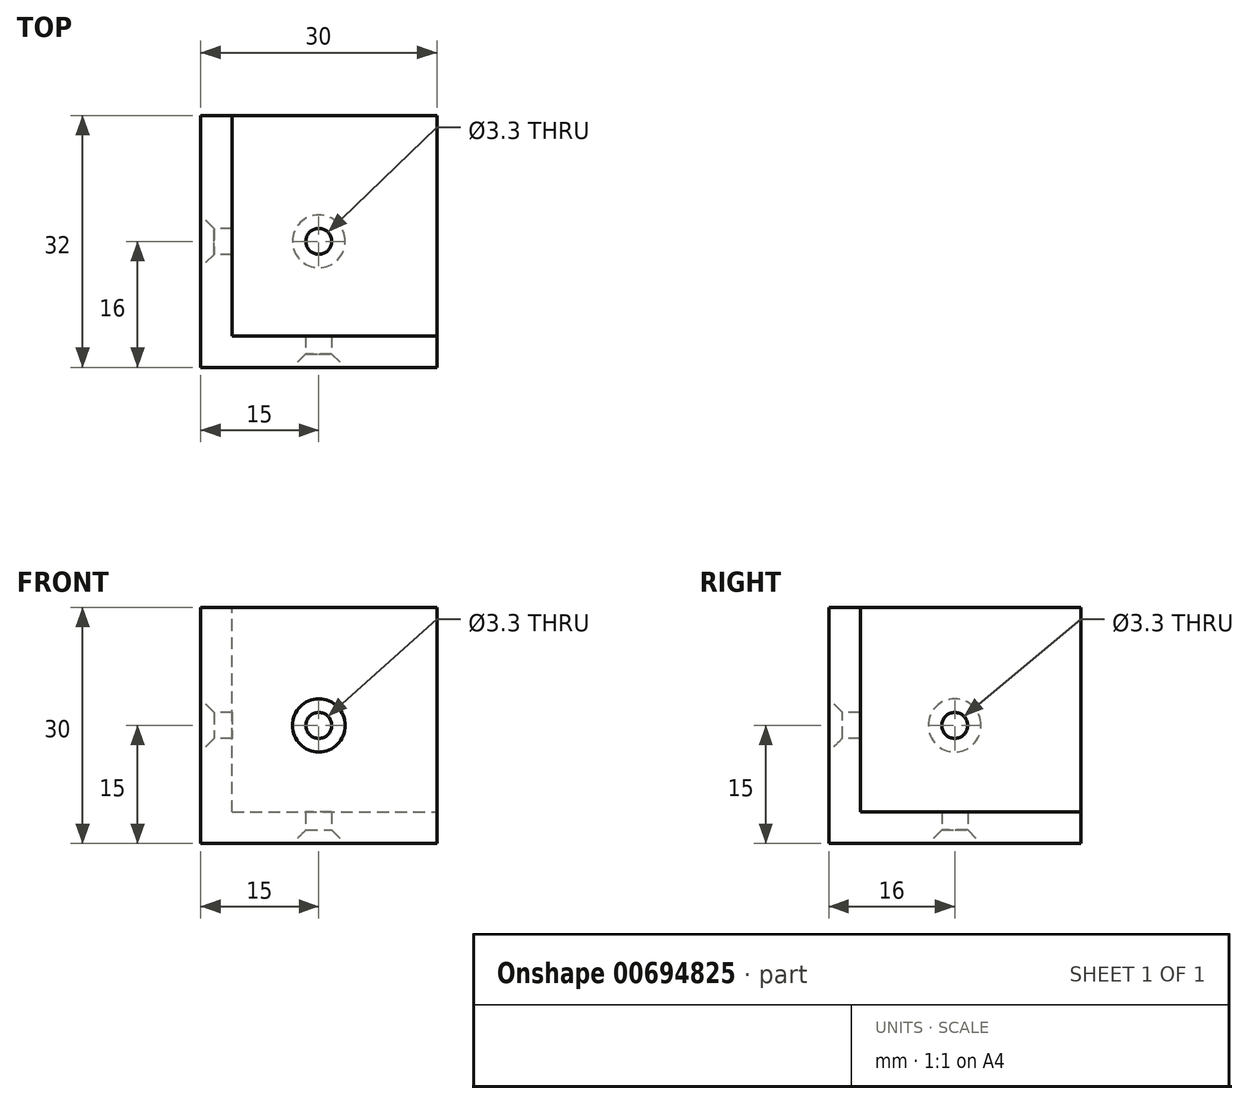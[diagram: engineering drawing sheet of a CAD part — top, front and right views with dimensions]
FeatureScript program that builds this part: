
annotation { "Feature Type Name" : "Feature", "Feature Type Description" : "" }
export const myFeature = defineFeature(function(context is Context, id is Id, definition is map)
    precondition{}
    {
        {
            var Q0;
            Q0=qCreatedBy(makeId("Front.planeOp"),FACE);
            var sketch = newSketch(context, id + "F0", { "sketchPlane" : qUnion([Q0])});
            skLineSegment(sketch, "E0.bottom", {"start": v(0, 0) * mm, "end": v(4, 0) * mm});
            skLineSegment(sketch, "E0.top", {"start": v(0, 30) * mm, "end": v(4, 30) * mm});
            skLineSegment(sketch, "E0.left", {"start": v(0, 0) * mm, "end": v(0, 30) * mm});
            skLineSegment(sketch, "E0.right", {"start": v(4, 4) * mm, "end": v(4, 30) * mm});
            skLineSegment(sketch, "E1.bottom", {"start": v(0, 0) * mm, "end": v(30, 0) * mm});
            skLineSegment(sketch, "E1.top", {"start": v(4, 4) * mm, "end": v(30, 4) * mm});
            skLineSegment(sketch, "E1.left", {"start": v(0, 0) * mm, "end": v(0, 4) * mm});
            skLineSegment(sketch, "E1.right", {"start": v(30, 0) * mm, "end": v(30, 4) * mm});
            skSolve(sketch);
        }
        {
            var Q0;
            Q0 = qSketchRegion(id + "F0", true);
            extrude(context, id + "F1", {"entities" : qUnion([Q0]), "depth" : 28 * mm, "offsetDistance" : 25 * mm});
        }
        {
            var Q0;
            Q0=makeQuery(id+"F1.opExtrude","CAP_FACE",FACE,{"disambiguationData":[OSD([sQuery(id+"F0.wireOp",EDGE,"E0.top"),sQuery(id+"F0.wireOp",EDGE,"E0.left"),sQuery(id+"F0.wireOp",EDGE,"E0.right"),sQuery(id+"F0.wireOp",EDGE,"E1.bottom"),sQuery(id+"F0.wireOp",EDGE,"E1.top"),sQuery(id+"F0.wireOp",EDGE,"E1.left"),sQuery(id+"F0.wireOp",EDGE,"E1.right")])],"isStart":false});
            var sketch = newSketch(context, id + "F2", { "sketchPlane" : qUnion([Q0])});
            skLineSegment(sketch, "E2.bottom", {"start": v(0, 0) * mm, "end": v(30, 0) * mm});
            skLineSegment(sketch, "E2.top", {"start": v(0, 30) * mm, "end": v(30, 30) * mm});
            skLineSegment(sketch, "E2.left", {"start": v(0, 0) * mm, "end": v(0, 30) * mm});
            skLineSegment(sketch, "E2.right", {"start": v(30, 0) * mm, "end": v(30, 30) * mm});
            skSolve(sketch);
        }
        {
            var Q0;
            Q0 = qSketchRegion(id + "F2", true);
            extrude(context, id + "F3", {"entities" : qUnion([Q0]), "operationType" : NewBodyOperationType.ADD, "depth" : 4 * mm, "offsetDistance" : 25 * mm});
        }
        {
            var Q0;
            Q0=makeQuery(id+"F3.opExtrude","CAP_FACE",FACE,{"disambiguationData":[OSD([sQuery(id+"F2.wireOp",EDGE,"E2.bottom"),sQuery(id+"F2.wireOp",EDGE,"E2.top"),sQuery(id+"F2.wireOp",EDGE,"E2.left"),sQuery(id+"F2.wireOp",EDGE,"E2.right")])],"isStart":false});
            var sketch = newSketch(context, id + "F4", { "sketchPlane" : qUnion([Q0])});
            skLineSegment(sketch, "E3", {"start": v(0, 0) * mm, "end": v(30, 30) * mm});
            skPoint(sketch, "E4", {"position": v(15, 15) * mm});
            skSolve(sketch);
        }
        {
            var Q0;
            Q0=sQuery(id+"F4.wireOp",VERTEX,"E4");
            var Q1;
            Q1=makeQuery(id+"F1.opExtrude","SWEPT_BODY",BODY,{"disambiguationData":[OSD([sQuery(id+"F0.wireOp",EDGE,"E0.top"),sQuery(id+"F0.wireOp",EDGE,"E0.left"),sQuery(id+"F0.wireOp",EDGE,"E0.right"),sQuery(id+"F0.wireOp",EDGE,"E1.bottom"),sQuery(id+"F0.wireOp",EDGE,"E1.top"),sQuery(id+"F0.wireOp",EDGE,"E1.left"),sQuery(id+"F0.wireOp",EDGE,"E1.right")])]});
            hole(context, id + "F5", {"style" : HoleStyle.C_SINK, "endStyle" : HoleEndStyle.BLIND, "standardTappedOrClearance" : lookupTablePath({ "standard" : "ISO", "fit" : "Normal", "size" : "M3", "type" : "Clearance" }), "standardBlindInLast" : lookupTablePath({ "fit" : "Standard", "standard" : "ISO", "size" : "M3", "type" : "Clearance" }), "holeDiameter" : 3.3 * mm, "cSinkDiameter" : 6.72 * mm, "cSinkAngle" : 90 * degree, "majorDiameter" : 5 * mm, "holeDepth" : 40 * mm, "isTappedThrough" : true, "tappedDepth" : 12 * mm, "tapClearance" : 3, "locations" : qUnion([Q0]), "scope" : qUnion([Q1])});
        }
        {
            var Q0;
            Q0=makeQuery(id+"F3.boolean.opBoolean","MERGE",FACE,{"derivedFrom":[makeQuery(id+"F1.opExtrude","SWEPT_FACE",FACE,{"disambiguationData":[OSD([sQuery(id+"F0.wireOp",EDGE,"E0.left"),sQuery(id+"F0.wireOp",EDGE,"E1.left")])]}),makeQuery(id+"F3.opExtrude","SWEPT_FACE",FACE,{"disambiguationData":[OSD([sQuery(id+"F2.wireOp",EDGE,"E2.left")])]})]});
            var sketch = newSketch(context, id + "F6", { "sketchPlane" : qUnion([Q0])});
            skLineSegment(sketch, "E5", {"start": v(0, 0) * mm, "end": v(32, 30) * mm});
            skPoint(sketch, "E6", {"position": v(16, 15) * mm});
            skSolve(sketch);
        }
        {
            var Q0;
            Q0=sQuery(id+"F6.wireOp",VERTEX,"E6");
            var Q1;
            Q1=makeQuery(id+"F1.opExtrude","SWEPT_BODY",BODY,{"disambiguationData":[OSD([sQuery(id+"F0.wireOp",EDGE,"E0.top"),sQuery(id+"F0.wireOp",EDGE,"E0.left"),sQuery(id+"F0.wireOp",EDGE,"E0.right"),sQuery(id+"F0.wireOp",EDGE,"E1.bottom"),sQuery(id+"F0.wireOp",EDGE,"E1.top"),sQuery(id+"F0.wireOp",EDGE,"E1.left"),sQuery(id+"F0.wireOp",EDGE,"E1.right")])]});
            hole(context, id + "F7", {"style" : HoleStyle.C_SINK, "endStyle" : HoleEndStyle.BLIND, "standardTappedOrClearance" : lookupTablePath({ "standard" : "ISO", "fit" : "Normal", "size" : "M3", "type" : "Clearance" }), "standardBlindInLast" : lookupTablePath({ "fit" : "Standard", "standard" : "ISO", "size" : "M3", "type" : "Clearance" }), "holeDiameter" : 3.3 * mm, "cSinkDiameter" : 6.72 * mm, "cSinkAngle" : 90 * degree, "majorDiameter" : 5 * mm, "holeDepth" : 40 * mm, "isTappedThrough" : true, "tappedDepth" : 12 * mm, "tapClearance" : 3, "locations" : qUnion([Q0]), "scope" : qUnion([Q1])});
        }
        {
            var Q0;
            Q0=makeQuery(id+"F3.boolean.opBoolean","MERGE",FACE,{"derivedFrom":[makeQuery(id+"F1.opExtrude","SWEPT_FACE",FACE,{"disambiguationData":[OSD([sQuery(id+"F0.wireOp",EDGE,"E1.bottom")])]}),makeQuery(id+"F3.opExtrude","SWEPT_FACE",FACE,{"disambiguationData":[OSD([sQuery(id+"F2.wireOp",EDGE,"E2.bottom")])]})]});
            var sketch = newSketch(context, id + "F8", { "sketchPlane" : qUnion([Q0])});
            skLineSegment(sketch, "E7", {"start": v(30, 0) * mm, "end": v(0, 32) * mm});
            skPoint(sketch, "E8", {"position": v(15, 16) * mm});
            skSolve(sketch);
        }
        {
            var Q0;
            Q0=sQuery(id+"F8.wireOp",VERTEX,"E8");
            var Q1;
            Q1=makeQuery(id+"F1.opExtrude","SWEPT_BODY",BODY,{"disambiguationData":[OSD([sQuery(id+"F0.wireOp",EDGE,"E0.top"),sQuery(id+"F0.wireOp",EDGE,"E0.left"),sQuery(id+"F0.wireOp",EDGE,"E0.right"),sQuery(id+"F0.wireOp",EDGE,"E1.bottom"),sQuery(id+"F0.wireOp",EDGE,"E1.top"),sQuery(id+"F0.wireOp",EDGE,"E1.left"),sQuery(id+"F0.wireOp",EDGE,"E1.right")])]});
            hole(context, id + "F9", {"style" : HoleStyle.C_SINK, "endStyle" : HoleEndStyle.BLIND, "standardTappedOrClearance" : lookupTablePath({ "standard" : "ISO", "fit" : "Normal", "size" : "M3", "type" : "Clearance" }), "standardBlindInLast" : lookupTablePath({ "fit" : "Standard", "standard" : "ISO", "size" : "M3", "type" : "Clearance" }), "holeDiameter" : 3.3 * mm, "cSinkDiameter" : 6.72 * mm, "cSinkAngle" : 90 * degree, "majorDiameter" : 5 * mm, "holeDepth" : 40 * mm, "isTappedThrough" : true, "tappedDepth" : 12 * mm, "tapClearance" : 3, "locations" : qUnion([Q0]), "scope" : qUnion([Q1])});
        }
    });
